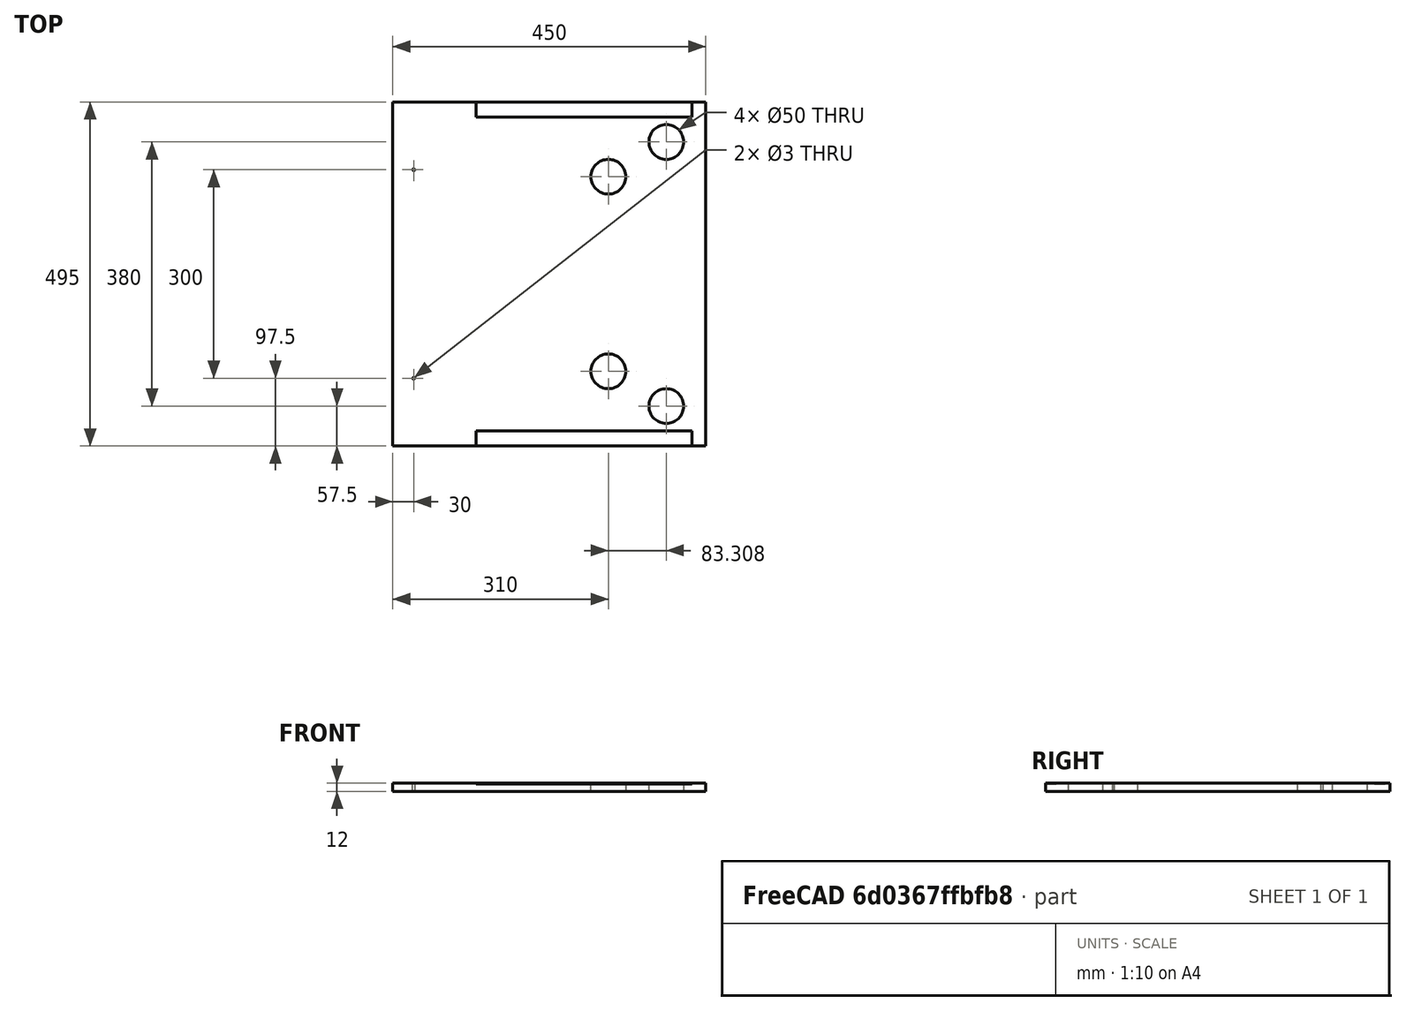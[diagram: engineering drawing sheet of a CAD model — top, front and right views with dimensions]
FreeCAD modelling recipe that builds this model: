
FCSTD DOCUMENT  (FreeCAD 0.20R29177 (Git))
Label: 8000_PRT_Floor
License: All rights reserved
LicenseURL: http://en.wikipedia.org/wiki/All_rights_reserved
objects: TechDraw::DrawViewDimension×15, Sketcher::SketchObject×5, PartDesign::Pocket×3, TechDraw::DrawViewPart×2, Spreadsheet::Sheet×1, TechDraw::DrawSVGTemplate×1, PartDesign::Pad×1, App::Part×1, PartDesign::Body×1, TechDraw::DrawPage×1
note: 14 computed .brp shape members not serialized (recipe doc carries the construction recipe); baked Part::Feature solids carry a one-line shape summary decoded from their .brp

FEATURE [Spreadsheet::Sheet] Spreadsheet
  cells = B2=BODY FLOOR; B3=Z=; C3(T)=12; D3=.T; E3=Thichness; B4=Y=; C4(Width)=495; D4=.W; E4=Width; B5=X=; C5(Depth)=450; D5=.D; E5=Depth
FEATURE [Sketcher::SketchObject] Sketch003  label="arrow"
  FullyConstrained = false
  MapMode = 5
  sketch-geometry (7):
    g0: LineSegment StartX=32.3501 StartY=274.69 StartZ=0 EndX=13.3739 EndY=266.182 EndZ=0
    g1: LineSegment StartX=13.3739 StartY=266.182 StartZ=0 EndX=32.3501 EndY=257.675 EndZ=0
    g2: LineSegment StartX=32.3501 StartY=257.675 StartZ=0 EndX=32.3501 EndY=263.308 EndZ=0
    g3: LineSegment StartX=32.3501 StartY=274.69 StartZ=0 EndX=32.3501 EndY=269.057 EndZ=0
    g4: LineSegment StartX=32.3501 StartY=269.057 StartZ=0 EndX=43.1376 EndY=269.057 EndZ=0
    g5: LineSegment StartX=43.1376 StartY=269.057 StartZ=0 EndX=43.1376 EndY=263.308 EndZ=0
    g6: LineSegment StartX=43.1376 StartY=263.308 StartZ=0 EndX=32.3501 EndY=263.308 EndZ=0
  constraints (15):
    c: Coincident(g1,g0)
    c: Coincident(g2,g1)
    c: Vertical(g2)
    c: Coincident(g3,g0)
    c: Vertical(g3)
    c: Coincident(g4,g3)
    c: Horizontal(g4)
    c: Coincident(g5,g4)
    c: Coincident(g6,g5)
    c: Coincident(g6,g2)
    c: Equal(g2,g3)
    c: Horizontal(g6)
    c: Vertical(g5)
    c: Equal(g1,g0)
    c: Vertical(g2,g3)
FEATURE [Sketcher::SketchObject] Sketch004
  FullyConstrained = false
  MapMode = 5
  sketch-geometry (16):
    g0: Circle CenterX=393.308 CenterY=437.5 CenterZ=0 NormalX=0 NormalY=0 NormalZ=1 AngleXU=0 Radius=25
    g1: Circle CenterX=393.308 CenterY=57.5 CenterZ=0 NormalX=0 NormalY=0 NormalZ=1 AngleXU=0 Radius=25
    g2: LineSegment StartX=393.308 StartY=437.5 StartZ=0 EndX=393.308 EndY=247.5 EndZ=0
    g3: LineSegment StartX=393.308 StartY=247.5 StartZ=0 EndX=393.308 EndY=57.5 EndZ=0
    g4: LineSegment StartX=310 StartY=247.5 StartZ=0 EndX=310 EndY=387.5 EndZ=0
    g5: LineSegment StartX=310 StartY=247.5 StartZ=0 EndX=310 EndY=107.5 EndZ=0
    g6: Circle CenterX=310 CenterY=107.5 CenterZ=0 NormalX=0 NormalY=0 NormalZ=1 AngleXU=0 Radius=25
    g7: Circle CenterX=310 CenterY=387.5 CenterZ=0 NormalX=0 NormalY=0 NormalZ=1 AngleXU=0 Radius=25
    g8: LineSegment StartX=0 StartY=0 StartZ=0 EndX=450 EndY=0 EndZ=0
    g9: LineSegment StartX=450 StartY=0 StartZ=0 EndX=450 EndY=495 EndZ=0
    g10: LineSegment StartX=450 StartY=495 StartZ=0 EndX=0 EndY=495 EndZ=0
    g11: LineSegment StartX=0 StartY=495 StartZ=0 EndX=0 EndY=0 EndZ=0
    g12: LineSegment StartX=0 StartY=495 StartZ=0 EndX=880.269 EndY=495 EndZ=0
    g13: LineSegment StartX=880.269 StartY=495 StartZ=0 EndX=880.269 EndY=475 EndZ=0
    g14: LineSegment StartX=880.269 StartY=475 StartZ=0 EndX=0 EndY=475 EndZ=0
    g15: LineSegment StartX=0 StartY=475 StartZ=0 EndX=0 EndY=495 EndZ=0
  constraints (42):
    c: Coincident(g2,g0)
    c: Coincident(g3,g2)
    c: Vertical(g2)
    c: Vertical(g3)
    c: Equal(g3,g2)
    c: Equal(g0,g1)
    c: Coincident(g1,g3)
    c: DistanceY(g1,g0) = 380  'D1'
    c: DistanceY(g-1,g2) = 247.5
    c: Diameter(g0) = 50
    c: Vertical(g4)
    c: Equal(g5,g4)
    c: Vertical(g5)
    c: Coincident(g5,g4)
    c: Horizontal(g4,g2)
    c: Coincident(g6,g5)
    c: Coincident(g7,g4)
    c: Equal(g6,g7)
    c: Diameter(g7) = 50
    c: DistanceY(g4,g4) = 140
    c: Coincident(g8,g9)
    c: Coincident(g9,g10)
    c: Coincident(g10,g11)
    c: Coincident(g11,g8)
    c: Horizontal(g8)
    c: Horizontal(g10)
    c: Vertical(g9)
    c: Vertical(g11)
    c: Coincident(g8,g-1)
    c: DistanceX(g10,g10) = 450
    c: DistanceY(g9,g9) = 495
    c: DistanceX(g6,g8) = 140
    c: Coincident(g12,g13)
    c: Coincident(g13,g14)
    c: Coincident(g14,g15)
    c: Coincident(g15,g12)
    c: Horizontal(g12)
    c: Horizontal(g14)
    c: Vertical(g13)
    c: Vertical(g15)
    c: DistanceY(g15,g15) = 20
    c: Coincident(g12,g10)
FEATURE [TechDraw::DrawSVGTemplate] Template
  EditableTexts = Designed_by_Name=RIP 2022 01 24; Drawing_number=800_PRT_Floor; FC-Date=2024 06 20; FC-SC=0,2; FC-SH=1; FC-Title=Cabinet Floor Fixtures; Subtitle=800_PRT_Floor; Weight=Weight
  Height = 210
  Orientation = 1
  Width = 297
FEATURE [Sketcher::SketchObject] Sketch005
  ExternalGeometry = -> [Sketch004]
  FullyConstrained = true
  MapMode = 5
  Support = -> [XY_Plane001]
  sketch-geometry (6):
    g0: LineSegment StartX=310 StartY=107.5 StartZ=0 EndX=310 EndY=247.5 EndZ=0
    g1: LineSegment StartX=310 StartY=247.5 StartZ=0 EndX=310 EndY=387.5 EndZ=0
    g2: Circle CenterX=30 CenterY=397.5 CenterZ=0 NormalX=0 NormalY=0 NormalZ=1 AngleXU=0 Radius=1.5
    g3: Circle CenterX=30 CenterY=97.5 CenterZ=0 NormalX=0 NormalY=0 NormalZ=1 AngleXU=0 Radius=1.5
    g4: LineSegment StartX=30 StartY=397.5 StartZ=0 EndX=30 EndY=247.5 EndZ=0
    g5: LineSegment StartX=30 StartY=247.5 StartZ=0 EndX=30 EndY=97.5 EndZ=0
  constraints (16):
    c: Coincident(g0,g-3)
    c: Vertical(g0)
    c: Coincident(g1,g0)
    c: Coincident(g1,g-4)
    c: Equal(g1,g0)
    c: Equal(g3,g2)
    c: Diameter(g2) = 3
    c: Coincident(g4,g2)
    c: Coincident(g5,g4)
    c: Coincident(g5,g3)
    c: Equal(g4,g5)
    c: Vertical(g5)
    c: Vertical(g4)
    c: Horizontal(g4,g0)
    c: DistanceY(g3,g2) = 300
    c: DistanceX(g-1,g3) = 30
FEATURE [Sketcher::SketchObject] Sketch006
  ExternalGeometry = -> [Sketch004]
  FullyConstrained = true
  MapMode = 5
  Support = -> [XY_Plane001]
  sketch-geometry (12):
    g0: LineSegment StartX=120 StartY=22 StartZ=0 EndX=430 EndY=22 EndZ=0
    g1: LineSegment StartX=430 StartY=22 StartZ=0 EndX=430 EndY=0 EndZ=0
    g2: LineSegment StartX=430 StartY=0 StartZ=0 EndX=120 EndY=0 EndZ=0
    g3: LineSegment StartX=120 StartY=0 StartZ=0 EndX=120 EndY=22 EndZ=0
    g4: LineSegment StartX=120 StartY=495 StartZ=0 EndX=430 EndY=495 EndZ=0
    g5: LineSegment StartX=430 StartY=495 StartZ=0 EndX=430 EndY=473 EndZ=0
    g6: LineSegment StartX=430 StartY=473 StartZ=0 EndX=120 EndY=473 EndZ=0
    g7: LineSegment StartX=120 StartY=473 StartZ=0 EndX=120 EndY=495 EndZ=0
    g8: LineSegment StartX=310 StartY=387.5 StartZ=0 EndX=310 EndY=247.5 EndZ=0
    g9: LineSegment StartX=310 StartY=247.5 StartZ=0 EndX=310 EndY=107.5 EndZ=0
    g10: LineSegment StartX=120 StartY=473 StartZ=0 EndX=120 EndY=247.5 EndZ=0
    g11: LineSegment StartX=120 StartY=247.5 StartZ=0 EndX=120 EndY=22 EndZ=0
  constraints (34):
    c: Coincident(g0,g1)
    c: Coincident(g1,g2)
    c: Coincident(g2,g3)
    c: Coincident(g3,g0)
    c: Horizontal(g0)
    c: Horizontal(g2)
    c: Vertical(g1)
    c: Vertical(g3)
    c: Coincident(g4,g5)
    c: Coincident(g5,g6)
    c: Coincident(g6,g7)
    c: Coincident(g7,g4)
    c: Horizontal(g4)
    c: Horizontal(g6)
    c: Vertical(g5)
    c: Vertical(g7)
    c: Vertical(g6,g0)
    c: Equal(g3,g7)
    c: Equal(g6,g0)
    c: DistanceY(g5,g5) = 22
    c: DistanceX(g4,g4) = 310
    c: Coincident(g8,g-4)
    c: Vertical(g8)
    c: Coincident(g9,g8)
    c: Coincident(g9,g-3)
    c: Equal(g9,g8)
    c: Coincident(g10,g6)
    c: Vertical(g10)
    c: Coincident(g11,g10)
    c: Coincident(g11,g0)
    c: Horizontal(g10,g8)
    c: Horizontal(g2,g-1)
    c: DistanceY(g1,g4) = 495
    c: DistanceX(g-1,g2) = 120
FEATURE [Sketcher::SketchObject] Sketch
  FullyConstrained = false
  MapMode = 2
  Support = -> [Part]
  expr: Constraints[5] = Spreadsheet.Depth
  expr: Constraints[6] = Spreadsheet.Width
  sketch-geometry (7):
    g0: LineSegment StartX=0 StartY=413.879 StartZ=0 EndX=0 EndY=495 EndZ=0
    g1: LineSegment StartX=0 StartY=495 StartZ=0 EndX=450 EndY=495 EndZ=0
    g2: LineSegment StartX=450 StartY=495 StartZ=0 EndX=450 EndY=0 EndZ=0
    g3: LineSegment StartX=450 StartY=0 StartZ=0 EndX=0 EndY=0 EndZ=0
    g4: LineSegment StartX=0 StartY=0 StartZ=0 EndX=0 EndY=413.879 EndZ=0
    g5: LineSegment StartX=0 StartY=0 StartZ=0 EndX=225 EndY=247.5 EndZ=0
    g6: LineSegment StartX=225 StartY=247.5 StartZ=0 EndX=450 EndY=495 EndZ=0
  constraints (18):
    c: Coincident(g1,g0)
    c: Horizontal(g1)
    c: Horizontal(g3)
    c: Coincident(g4,g3)
    c: Coincident(g3,g2)
    c: Distance(g1) = 450
    c: DistanceY(g2,g2) = 495
    c: Coincident(g1,g2)
    c: Coincident(g5,g3)
    c: Coincident(g6,g1)
    c: Equal(g6,g5)
    c: Coincident(g5,g6)
    c: Parallel(g5,g6)
    c: Vertical(g0)
    c: Vertical(g2)
    c: Coincident(g4,g0)
    c: Vertical(g4)
    c: Coincident(g3,g-1)
FEATURE [PartDesign::Pad] Pad
  AllowMultiFace = false
  Direction = (0,0,1)
  Length = 12
  Length2 = 100
  Profile = -> Sketch
  Reversed = true
  Type = 0
FEATURE [App::Part] Part
  Group = -> [PadBody]
  License = CC BY 3.0
  LicenseURL = http://creativecommons.org/licenses/by/3.0/
  Origin = -> Origin
FEATURE [PartDesign::Body] PadBody
  Group = -> [Sketch,Pad,Sketch003,Sketch004,Pocket001,Sketch005,Pocket,Sketch006,Pocket002]
  Origin = -> Origin001
  Tip = -> Pocket002
FEATURE [PartDesign::Pocket] Pocket001
  BaseFeature = -> Pad
  Direction = (0,0,-1)
  Length = 20
  Length2 = 100
  Profile = -> Sketch004
  Type = 0
FEATURE [TechDraw::DrawPage] Page
  KeepUpdated = true
  NextBalloonIndex = 2
  ProjectionType = 0
  Template = -> Template
  Views = -> [View,Dimension,Dimension001,View001,Dimension011,Dimension012,Dimension015,Dimension016,Dimension017,Dimension018,Dimension019,Dimension020,Dimension021,Dimension022,Dimension023,Dimension024,Dimension025]
FEATURE [TechDraw::DrawViewPart] View
  CoarseView = false
  Direction = (0,0,1)
  Focus = 100
  HardHidden = false
  IsoCount = 0
  IsoHidden = false
  IsoVisible = false
  LockPosition = false
  Perspective = false
  Rotation = 0
  Scale = 0.2
  ScaleType = 2
  SeamHidden = false
  SeamVisible = true
  SmoothHidden = false
  SmoothVisible = true
  Source = -> [PadBody]
  X = 76.2164
  XDirection = (0,-1,0)
  Y = 132.992
FEATURE [TechDraw::DrawViewDimension] Dimension
  AngleOverride = false
  Arbitrary = false
  ArbitraryTolerances = false
  EqualTolerance = true
  ExtensionAngle = 0
  FormatSpec = %.2f
  FormatSpecOverTolerance = %+.2f
  FormatSpecUnderTolerance = %+.2f
  Inverted = false
  LineAngle = 0
  LockPosition = false
  MeasureType = 1
  OverTolerance = 0
  References2D = -> [View]
  Rotation = 0
  ScaleType = 0
  TheoreticalExact = false
  Type = 2
  UnderTolerance = 0
  X = 62.2508
  Y = 1.79508
FEATURE [TechDraw::DrawViewDimension] Dimension001
  AngleOverride = false
  Arbitrary = false
  ArbitraryTolerances = false
  EqualTolerance = true
  ExtensionAngle = 0
  FormatSpec = %.2f
  FormatSpecOverTolerance = %+.2f
  FormatSpecUnderTolerance = %+.2f
  Inverted = false
  LineAngle = 0
  LockPosition = false
  MeasureType = 1
  OverTolerance = 0
  References2D = -> [View]
  Rotation = 0
  ScaleType = 0
  TheoreticalExact = false
  Type = 1
  UnderTolerance = 0
  X = 1.22032
  Y = -56.6641
FEATURE [TechDraw::DrawViewPart] View001
  CoarseView = false
  Direction = (0,0,1)
  Focus = 100
  HardHidden = false
  IsoCount = 0
  IsoHidden = false
  IsoVisible = false
  LockPosition = false
  Perspective = false
  Rotation = 0
  Scale = 0.2
  ScaleType = 2
  SeamHidden = false
  SeamVisible = true
  SmoothHidden = false
  SmoothVisible = true
  Source = -> [Part]
  X = 220.592
  XDirection = (0,-1,0)
  Y = 133.909
FEATURE [PartDesign::Pocket] Pocket
  BaseFeature = -> Pocket001
  Direction = (0,0,-1)
  Length = 5
  Length2 = 5
  Profile = -> Sketch005
  ReferenceAxis = -> Sketch005 [N_Axis]
  Type = 1
FEATURE [PartDesign::Pocket] Pocket002
  BaseFeature = -> Pocket
  Direction = (0,0,-1)
  Length = 1
  Length2 = 5
  Profile = -> Sketch006
  ReferenceAxis = -> Sketch006 [N_Axis]
  Type = 0
FEATURE [TechDraw::DrawViewDimension] Dimension011
  AngleOverride = false
  Arbitrary = false
  ArbitraryTolerances = false
  EqualTolerance = true
  ExtensionAngle = 0
  FormatSpec = %.2f
  FormatSpecOverTolerance = %+.2f
  FormatSpecUnderTolerance = %+.2f
  Inverted = false
  LineAngle = 0
  LockPosition = false
  MeasureType = 1
  OverTolerance = 0
  References2D = -> [View]
  Rotation = 0
  ScaleType = 0
  TheoreticalExact = false
  Type = 2
  UnderTolerance = 0
  X = -62.3816
  Y = 4.89658
FEATURE [TechDraw::DrawViewDimension] Dimension012
  AngleOverride = false
  Arbitrary = false
  ArbitraryTolerances = false
  EqualTolerance = true
  ExtensionAngle = 0
  FormatSpec = %.2f
  FormatSpecOverTolerance = %+.2f
  FormatSpecUnderTolerance = %+.2f
  Inverted = false
  LineAngle = 0
  LockPosition = false
  MeasureType = 1
  OverTolerance = 0
  References2D = -> [View001]
  Rotation = 0
  ScaleType = 0
  TheoreticalExact = false
  Type = 1
  UnderTolerance = 0
  X = -2.76035
  Y = 8.14572
FEATURE [TechDraw::DrawViewDimension] Dimension015
  AngleOverride = false
  Arbitrary = false
  ArbitraryTolerances = false
  EqualTolerance = true
  ExtensionAngle = 0
  FormatSpec = %.2f
  FormatSpecOverTolerance = %+.2f
  FormatSpecUnderTolerance = %+.2f
  Inverted = false
  LineAngle = 0
  LockPosition = false
  MeasureType = 1
  OverTolerance = 0
  References2D = -> [View001]
  Rotation = 0
  ScaleType = 0
  TheoreticalExact = false
  Type = 2
  UnderTolerance = 0
  X = 57.3225
  Y = 11.4215
FEATURE [TechDraw::DrawViewDimension] Dimension016
  AngleOverride = false
  Arbitrary = false
  ArbitraryTolerances = false
  EqualTolerance = true
  ExtensionAngle = 0
  FormatSpec = %.2f
  FormatSpecOverTolerance = %+.2f
  FormatSpecUnderTolerance = %+.2f
  Inverted = false
  LineAngle = 0
  LockPosition = false
  MeasureType = 1
  OverTolerance = 0
  References2D = -> [View001]
  Rotation = 0
  ScaleType = 0
  TheoreticalExact = false
  Type = 2
  UnderTolerance = 0
  X = -65.0777
  Y = -27.8039
FEATURE [TechDraw::DrawViewDimension] Dimension017
  AngleOverride = false
  Arbitrary = false
  ArbitraryTolerances = false
  EqualTolerance = true
  ExtensionAngle = 0
  FormatSpec = %.2f
  FormatSpecOverTolerance = %+.2f
  FormatSpecUnderTolerance = %+.2f
  Inverted = false
  LineAngle = 0
  LockPosition = false
  MeasureType = 1
  OverTolerance = 0
  References2D = -> [View001]
  Rotation = 0
  ScaleType = 0
  TheoreticalExact = false
  Type = 1
  UnderTolerance = 0
  X = -2.097
  Y = -58.6683
FEATURE [TechDraw::DrawViewDimension] Dimension018
  AngleOverride = false
  Arbitrary = false
  ArbitraryTolerances = false
  EqualTolerance = true
  ExtensionAngle = 0
  FormatSpec = %.2f
  FormatSpecOverTolerance = %+.2f
  FormatSpecUnderTolerance = %+.2f
  Inverted = false
  LineAngle = 0
  LockPosition = false
  MeasureType = 1
  OverTolerance = 0
  References2D = -> [View001]
  Rotation = 0
  ScaleType = 0
  TheoreticalExact = false
  Type = 1
  UnderTolerance = 0
  X = 4.49358
  Y = 59.5282
FEATURE [TechDraw::DrawViewDimension] Dimension019
  AngleOverride = false
  Arbitrary = false
  ArbitraryTolerances = false
  EqualTolerance = true
  ExtensionAngle = 0
  FormatSpec = %.2f
  FormatSpecOverTolerance = %+.2f
  FormatSpecUnderTolerance = %+.2f
  Inverted = false
  LineAngle = 0
  LockPosition = false
  MeasureType = 1
  OverTolerance = 0
  References2D = -> [View001]
  Rotation = 0
  ScaleType = 0
  TheoreticalExact = false
  Type = 2
  UnderTolerance = 0
  X = -66.709
  Y = 57.5583
FEATURE [TechDraw::DrawViewDimension] Dimension020
  AngleOverride = false
  Arbitrary = false
  ArbitraryTolerances = false
  EqualTolerance = true
  ExtensionAngle = 0
  FormatSpec = %.2f
  FormatSpecOverTolerance = %+.2f
  FormatSpecUnderTolerance = %+.2f
  Inverted = false
  LineAngle = 0
  LockPosition = false
  MeasureType = 1
  OverTolerance = 0
  References2D = -> [View001]
  Rotation = 0
  ScaleType = 0
  TheoreticalExact = false
  Type = 2
  UnderTolerance = 0
  X = -5.03281
  Y = 33.9993
FEATURE [TechDraw::DrawViewDimension] Dimension021
  AngleOverride = false
  Arbitrary = false
  ArbitraryTolerances = false
  EqualTolerance = true
  ExtensionAngle = 0
  FormatSpec = %.2f
  FormatSpecOverTolerance = %+.2f
  FormatSpecUnderTolerance = %+.2f
  Inverted = false
  LineAngle = 0
  LockPosition = false
  MeasureType = 1
  OverTolerance = 0
  References2D = -> [View001]
  Rotation = 0
  ScaleType = 0
  TheoreticalExact = false
  Type = 2
  UnderTolerance = 0
  X = 37.8325
  Y = -59.4277
FEATURE [TechDraw::DrawViewDimension] Dimension022
  AngleOverride = false
  Arbitrary = false
  ArbitraryTolerances = false
  EqualTolerance = true
  ExtensionAngle = 0
  FormatSpec = ⌀%.2f
  FormatSpecOverTolerance = %+.2f
  FormatSpecUnderTolerance = %+.2f
  Inverted = false
  LineAngle = 0
  LockPosition = false
  MeasureType = 1
  OverTolerance = 0
  References2D = -> [View]
  Rotation = 0
  ScaleType = 0
  TheoreticalExact = false
  Type = 5
  UnderTolerance = 0
  X = -10.9843
  Y = 37.6961
FEATURE [TechDraw::DrawViewDimension] Dimension023
  AngleOverride = false
  Arbitrary = false
  ArbitraryTolerances = false
  EqualTolerance = true
  ExtensionAngle = 0
  FormatSpec = ⌀%.2f
  FormatSpecOverTolerance = %+.2f
  FormatSpecUnderTolerance = %+.2f
  Inverted = false
  LineAngle = 0
  LockPosition = false
  MeasureType = 1
  OverTolerance = 0
  References2D = -> [View]
  Rotation = 0
  ScaleType = 0
  TheoreticalExact = false
  Type = 5
  UnderTolerance = 0
  X = -10.2354
  Y = 21.9686
FEATURE [TechDraw::DrawViewDimension] Dimension024
  AngleOverride = false
  Arbitrary = false
  ArbitraryTolerances = false
  EqualTolerance = true
  ExtensionAngle = 0
  FormatSpec = %.2f
  FormatSpecOverTolerance = %+.2f
  FormatSpecUnderTolerance = %+.2f
  Inverted = false
  LineAngle = 0
  LockPosition = false
  MeasureType = 1
  OverTolerance = 0
  References2D = -> [View]
  Rotation = 0
  ScaleType = 0
  TheoreticalExact = false
  Type = 2
  UnderTolerance = 0
  X = 58.5293
  Y = 55.5326
FEATURE [TechDraw::DrawViewDimension] Dimension025
  AngleOverride = false
  Arbitrary = false
  ArbitraryTolerances = false
  EqualTolerance = true
  ExtensionAngle = 0
  FormatSpec = ⌀%.2f
  FormatSpecOverTolerance = %+.2f
  FormatSpecUnderTolerance = %+.2f
  Inverted = false
  LineAngle = 0
  LockPosition = false
  MeasureType = 1
  OverTolerance = 0
  References2D = -> [View]
  Rotation = 0
  ScaleType = 0
  TheoreticalExact = false
  Type = 5
  UnderTolerance = 0
  X = 13.5223
  Y = -31.2054
